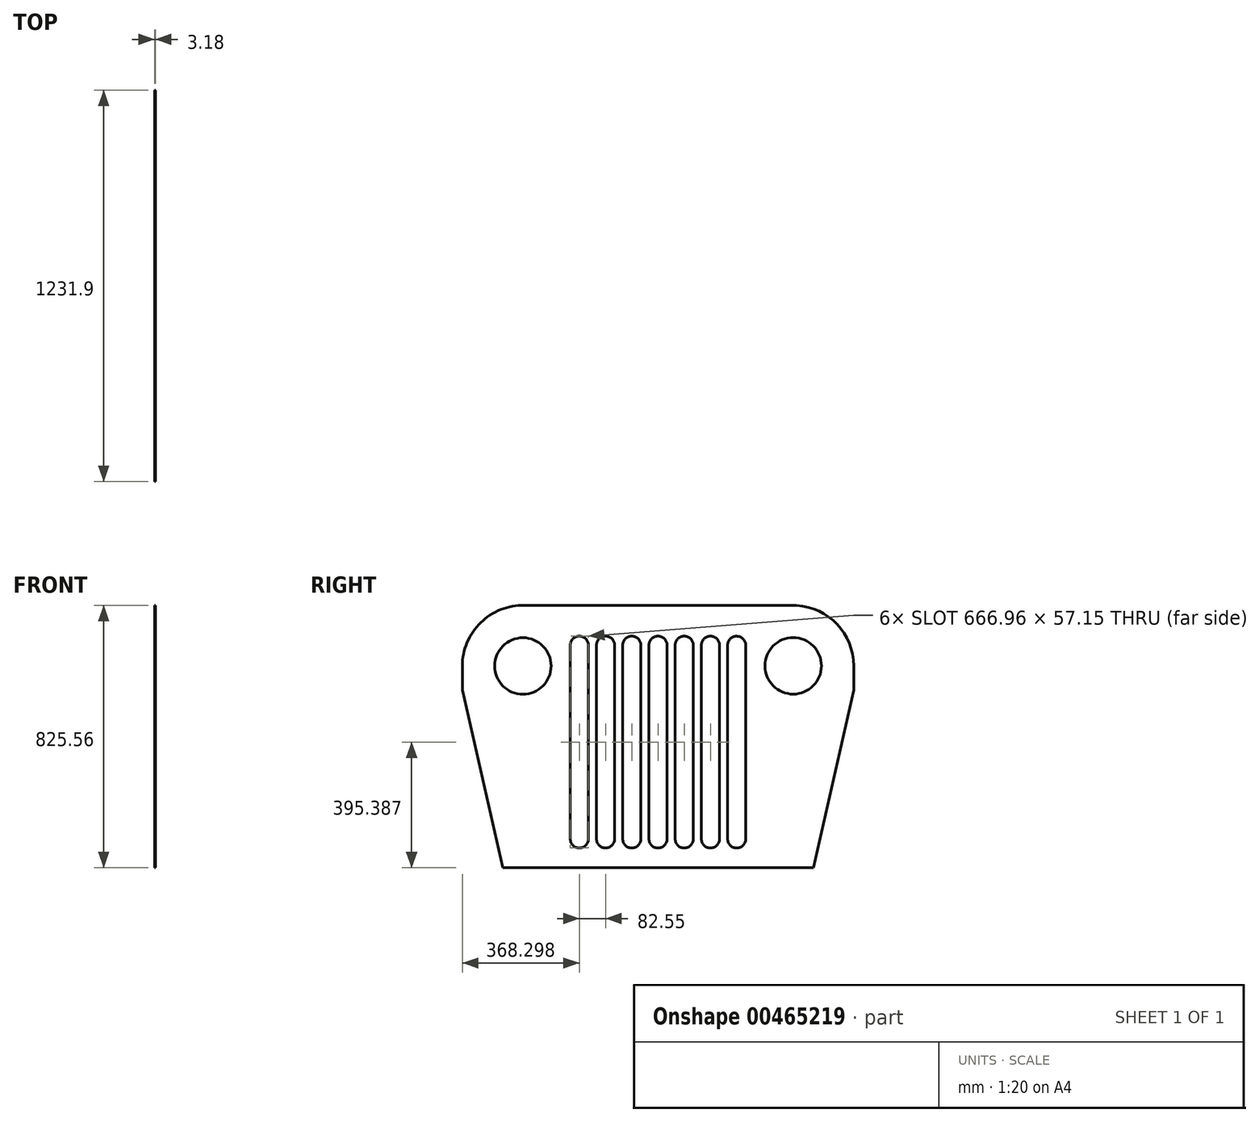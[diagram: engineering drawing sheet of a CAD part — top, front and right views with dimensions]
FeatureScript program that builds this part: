
annotation { "Feature Type Name" : "Feature", "Feature Type Description" : "" }
export const myFeature = defineFeature(function(context is Context, id is Id, definition is map)
    precondition{}
    {
        {
            var Q0;
            Q0=qCreatedBy(makeId("Right.planeOp"),FACE);
            var sketch = newSketch(context, id + "F0", { "sketchPlane" : qUnion([Q0])});
            skArc(sketch, "E0", {"start": v(640.99, 635) * mm, "mid": v(589.2, 765.9) * mm, "end": v(461.64, 825.5) * mm});
            skArc(sketch, "E1", {"start": v(-590.91, 635) * mm, "mid": v(-533.37, 771.46) * mm, "end": v(-395.49, 825.5) * mm});
            skLineSegment(sketch, "E2", {"start": v(461.64, 825.5) * mm, "end": v(-395.49, 825.5) * mm});
            skLineSegment(sketch, "E3", {"start": v(640.99, 558.8) * mm, "end": v(513.99, 0) * mm});
            skLineSegment(sketch, "E4", {"start": v(-463.91, 0) * mm, "end": v(-590.91, 558.8) * mm});
            skLineSegment(sketch, "E5", {"start": v(640.99, 635) * mm, "end": v(640.99, 558.8) * mm});
            skLineSegment(sketch, "E6", {"start": v(-590.91, 635) * mm, "end": v(-590.91, 558.8) * mm});
            skLineSegment(sketch, "E7", {"start": v(301.26, 700.08) * mm, "end": v(301.26, 90.48) * mm});
            skLineSegment(sketch, "E8", {"start": v(244.11, 700.26) * mm, "end": v(244.11, 90.45) * mm});
            skArc(sketch, "E9", {"start": v(301.26, 700.08) * mm, "mid": v(272.78, 728.66) * mm, "end": v(244.11, 700.26) * mm});
            skArc(sketch, "E10", {"start": v(301.26, 90.48) * mm, "mid": v(272.7, 61.9) * mm, "end": v(244.11, 90.45) * mm});
            skCircle(sketch, "E11", {"center": v(450.49, 635.33) * mm, "radius": 88.9 * mm});
            skCircle(sketch, "E12", {"center": v(-400.35, 635) * mm, "radius": 88.9 * mm});
            skLineSegment(sketch, "E13", {"start": v(218.71, 700.3) * mm, "end": v(218.71, 90.48) * mm});
            skLineSegment(sketch, "E14", {"start": v(161.56, 700.3) * mm, "end": v(161.56, 90.48) * mm});
            skArc(sketch, "E15", {"start": v(218.71, 700.3) * mm, "mid": v(190.14, 728.87) * mm, "end": v(161.56, 700.3) * mm});
            skArc(sketch, "E16", {"start": v(218.71, 90.48) * mm, "mid": v(190.14, 61.9) * mm, "end": v(161.56, 90.48) * mm});
            skLineSegment(sketch, "E17", {"start": v(136.16, 700.26) * mm, "end": v(136.16, 90.45) * mm});
            skLineSegment(sketch, "E18", {"start": v(79.01, 700.26) * mm, "end": v(79.01, 90.45) * mm});
            skArc(sketch, "E19", {"start": v(136.16, 700.26) * mm, "mid": v(107.59, 728.84) * mm, "end": v(79.01, 700.26) * mm});
            skArc(sketch, "E20", {"start": v(136.16, 90.45) * mm, "mid": v(107.59, 61.87) * mm, "end": v(79.01, 90.45) * mm});
            skLineSegment(sketch, "E21", {"start": v(53.61, 700.3) * mm, "end": v(53.61, 90.48) * mm});
            skLineSegment(sketch, "E22", {"start": v(-3.54, 700.3) * mm, "end": v(-3.54, 90.48) * mm});
            skArc(sketch, "E23", {"start": v(53.61, 700.3) * mm, "mid": v(25.04, 728.87) * mm, "end": v(-3.54, 700.3) * mm});
            skArc(sketch, "E24", {"start": v(53.61, 90.48) * mm, "mid": v(25.04, 61.9) * mm, "end": v(-3.54, 90.48) * mm});
            skLineSegment(sketch, "E25", {"start": v(-28.94, 700.3) * mm, "end": v(-28.94, 90.48) * mm});
            skLineSegment(sketch, "E26", {"start": v(-86.09, 700.3) * mm, "end": v(-86.09, 90.48) * mm});
            skArc(sketch, "E27", {"start": v(-28.94, 700.3) * mm, "mid": v(-57.51, 728.87) * mm, "end": v(-86.09, 700.3) * mm});
            skArc(sketch, "E28", {"start": v(-28.94, 90.48) * mm, "mid": v(-57.51, 61.9) * mm, "end": v(-86.09, 90.48) * mm});
            skLineSegment(sketch, "E29", {"start": v(-111.49, 700.33) * mm, "end": v(-111.49, 90.51) * mm});
            skLineSegment(sketch, "E30", {"start": v(-168.64, 700.33) * mm, "end": v(-168.64, 90.51) * mm});
            skArc(sketch, "E31", {"start": v(-111.49, 700.33) * mm, "mid": v(-140.06, 728.9) * mm, "end": v(-168.64, 700.33) * mm});
            skArc(sketch, "E32", {"start": v(-111.49, 90.51) * mm, "mid": v(-140.06, 61.94) * mm, "end": v(-168.64, 90.51) * mm});
            skLineSegment(sketch, "E33", {"start": v(-194.04, 700.3) * mm, "end": v(-194.04, 90.48) * mm});
            skLineSegment(sketch, "E34", {"start": v(-251.19, 700.3) * mm, "end": v(-251.19, 90.48) * mm});
            skArc(sketch, "E35", {"start": v(-194.04, 700.3) * mm, "mid": v(-222.61, 728.87) * mm, "end": v(-251.19, 700.3) * mm});
            skArc(sketch, "E36", {"start": v(-194.04, 90.48) * mm, "mid": v(-222.61, 61.9) * mm, "end": v(-251.19, 90.48) * mm});
            skLineSegment(sketch, "E37", {"start": v(513.99, 0) * mm, "end": v(-463.91, 0) * mm});
            skLineSegment(sketch, "E38", {"start": v(603.75, 1117.6) * mm, "end": v(-595.4, 1117.6) * mm});
            skSolve(sketch);
        }
        {
            var Q0;
            Q0=makeQuery(id+"F0.imprint","IMPRINT",FACE,{"disambiguationData":[TD([[makeQuery(id+"F0.imprint","IMPRINT",EDGE,{"derivedFrom":sQuery(id+"F0.wireOp",EDGE,"E0")}),1.0]])]});
            extrude(context, id + "F1", {"entities" : qUnion([Q0]), "depth" : 3.17 * mm});
        }
    });
